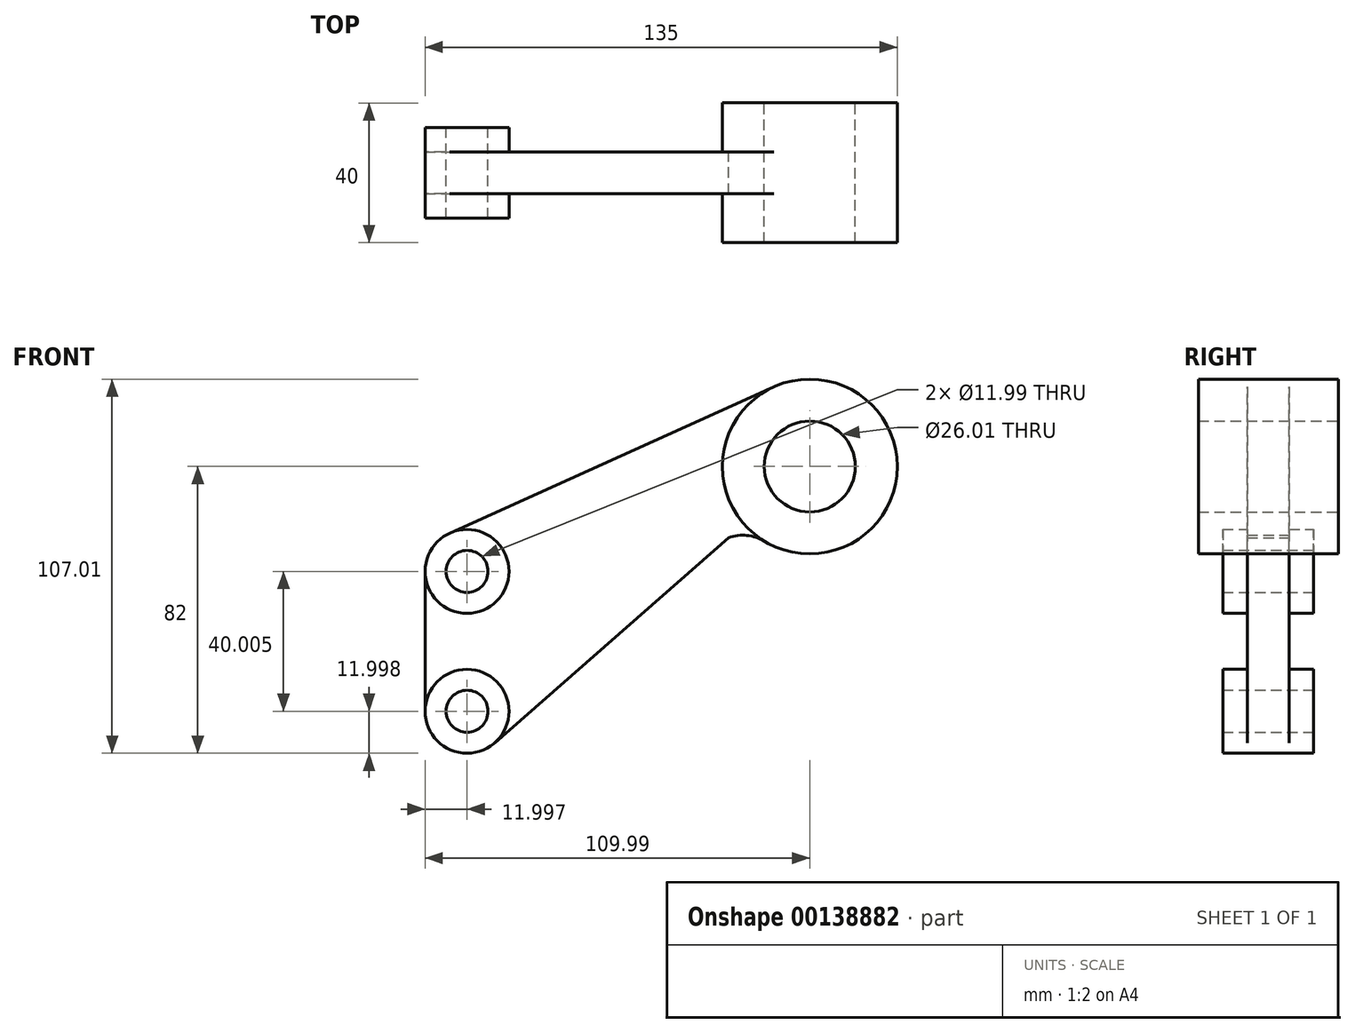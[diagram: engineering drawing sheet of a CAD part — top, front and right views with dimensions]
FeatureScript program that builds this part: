
annotation { "Feature Type Name" : "Feature", "Feature Type Description" : "" }
export const myFeature = defineFeature(function(context is Context, id is Id, definition is map)
    precondition{}
    {
        {
            var Q0;
            Q0=qCreatedBy(makeId("Front.planeOp"),FACE);
            var sketch = newSketch(context, id + "F0", { "sketchPlane" : qUnion([Q0])});
            skCircle(sketch, "E0", {"center": v(0, 0) * mm, "radius": 25 * mm});
            skCircle(sketch, "E1", {"center": v(0, 0) * mm, "radius": 13 * mm});
            skCircle(sketch, "E2", {"center": v(-98, -70) * mm, "radius": 12 * mm});
            skCircle(sketch, "E3", {"center": v(-98, -70) * mm, "radius": 6 * mm});
            skCircle(sketch, "E4", {"center": v(-98, -30) * mm, "radius": 12 * mm});
            skCircle(sketch, "E5", {"center": v(-98, -30) * mm, "radius": 6 * mm});
            skLineSegment(sketch, "E6", {"start": v(-102.93, -19.06) * mm, "end": v(-10.3, 22.79) * mm});
            skLineSegment(sketch, "E7", {"start": v(-110, -30) * mm, "end": v(-110, -70) * mm});
            skArc(sketch, "E8", {"start": v(-12.95, -21.4) * mm, "mid": v(-17.97, -19.72) * mm, "end": v(-23.22, -20.37) * mm});
            skLineSegment(sketch, "E9", {"start": v(-19.16, -31.65) * mm, "end": v(0, 0) * mm, "construction": true});
            skLineSegment(sketch, "E10", {"start": v(-90.08, -79.02) * mm, "end": v(-23.22, -20.37) * mm});
            skLineSegment(sketch, "E11", {"start": v(-23.22, -20.37) * mm, "end": v(0, 0) * mm, "construction": true});
            skSolve(sketch);
        }
        {
            var Q0;
            Q0=makeQuery(id+"F0.imprint","IMPRINT",FACE,{"disambiguationData":[TD([[makeQuery(id+"F0.imprint","IMPRINT",EDGE,{"derivedFrom":sQuery(id+"F0.wireOp",EDGE,"E1")}),-1.0]])]});
            extrude(context, id + "F1", {"entities" : qUnion([Q0]), "endBound" : BoundingType.SYMMETRIC, "depth" : 40 * mm});
        }
        {
            var Q0;
            {var subQ0=sQuery(id+"F0.wireOp",EDGE,"E6");Q0=makeQuery(id+"F0.imprint","IMPRINT",FACE,{"disambiguationData":[TD([[makeQuery(id+"F0.imprint","IMPRINT",EDGE,{"derivedFrom":subQ0}),-1.0]])]});}
            extrude(context, id + "F2", {"entities" : qUnion([Q0]), "operationType" : NewBodyOperationType.ADD, "endBound" : BoundingType.SYMMETRIC, "depth" : 12 * mm});
        }
        {
            var Q0;
            Q0=makeQuery(id+"F0.imprint","IMPRINT",FACE,{"disambiguationData":[TD([[makeQuery(id+"F0.imprint","IMPRINT",EDGE,{"derivedFrom":sQuery(id+"F0.wireOp",EDGE,"E5")}),-1.0]])]});
            var Q1;
            Q1=makeQuery(id+"F0.imprint","IMPRINT",FACE,{"disambiguationData":[TD([[makeQuery(id+"F0.imprint","IMPRINT",EDGE,{"derivedFrom":sQuery(id+"F0.wireOp",EDGE,"E3")}),-1.0]])]});
            extrude(context, id + "F3", {"entities" : qUnion([Q0, Q1]), "operationType" : NewBodyOperationType.ADD, "endBound" : BoundingType.SYMMETRIC, "depth" : 26 * mm});
        }
    });
